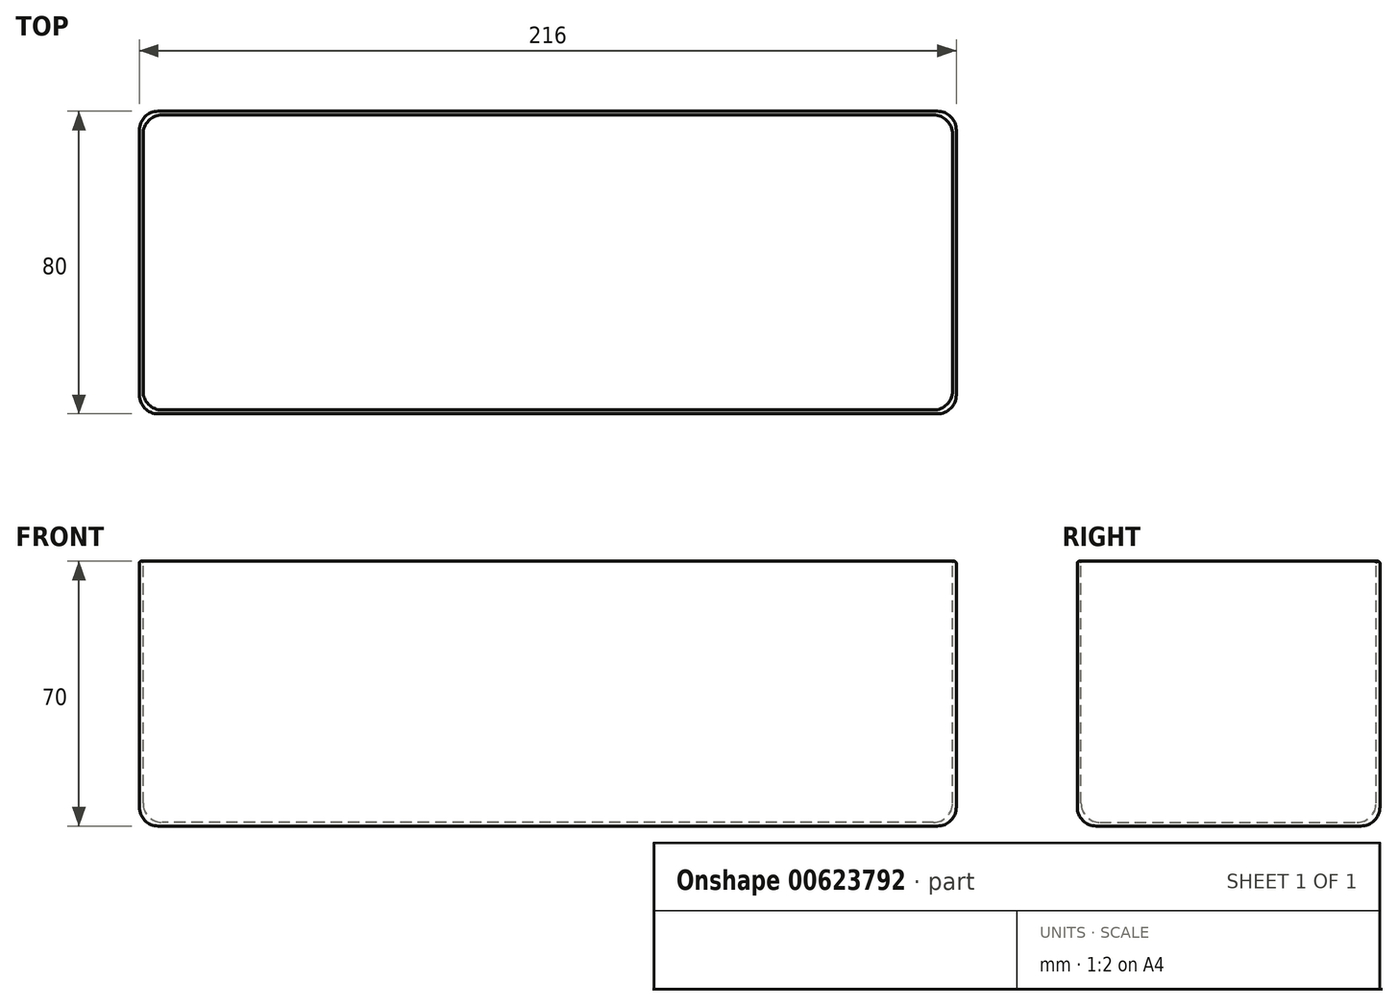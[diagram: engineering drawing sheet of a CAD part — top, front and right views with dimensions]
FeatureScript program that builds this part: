
annotation { "Feature Type Name" : "Feature", "Feature Type Description" : "" }
export const myFeature = defineFeature(function(context is Context, id is Id, definition is map)
    precondition{}
    {
        {
            var Q0;
            Q0=qCreatedBy(makeId("Top.planeOp"),FACE);
            var sketch = newSketch(context, id + "F0", { "sketchPlane" : qUnion([Q0])});
            skLineSegment(sketch, "E0.bottom", {"start": v(108, -40) * mm, "end": v(-108, -40) * mm});
            skLineSegment(sketch, "E0.top", {"start": v(108, 40) * mm, "end": v(-108, 40) * mm});
            skLineSegment(sketch, "E0.left", {"start": v(108, -40) * mm, "end": v(108, 40) * mm});
            skLineSegment(sketch, "E0.right", {"start": v(-108, -40) * mm, "end": v(-108, 40) * mm});
            skPoint(sketch, "E0.middle", {"position": v(0, 0) * mm});
            skSolve(sketch);
        }
        {
            var Q0;
            Q0=makeQuery(id+"F0.imprint","IMPRINT",FACE,{"disambiguationData":[TD([[makeQuery(id+"F0.imprint","IMPRINT",EDGE,{"derivedFrom":sQuery(id+"F0.wireOp",EDGE,"E0.bottom")}),-1.0]])]});
            extrude(context, id + "F1", {"entities" : qUnion([Q0]), "depth" : 70 * mm, "offsetDistance" : 25 * mm});
        }
        {
            var Q0;
            Q0=makeQuery(id+"F1.opExtrude","CAP_FACE",FACE,{"disambiguationData":[OSD([sQuery(id+"F0.wireOp",EDGE,"E0.bottom"),sQuery(id+"F0.wireOp",EDGE,"E0.top"),sQuery(id+"F0.wireOp",EDGE,"E0.left"),sQuery(id+"F0.wireOp",EDGE,"E0.right")])],"isStart":false});
            var sketch = newSketch(context, id + "F2", { "sketchPlane" : qUnion([Q0])});
            skLineSegment(sketch, "E1.bottom", {"start": v(107, -39) * mm, "end": v(-107, -39) * mm});
            skLineSegment(sketch, "E1.top", {"start": v(107, 39) * mm, "end": v(-107, 39) * mm});
            skLineSegment(sketch, "E1.left", {"start": v(107, -39) * mm, "end": v(107, 39) * mm});
            skLineSegment(sketch, "E1.right", {"start": v(-107, -39) * mm, "end": v(-107, 39) * mm});
            skPoint(sketch, "E1.middle", {"position": v(0, 0) * mm});
            skSolve(sketch);
        }
        {
            var Q0;
            Q0=makeQuery(id+"F2.imprint","IMPRINT",FACE,{"disambiguationData":[TD([[makeQuery(id+"F2.imprint","IMPRINT",EDGE,{"derivedFrom":sQuery(id+"F2.wireOp",EDGE,"E1.bottom")}),-1.0]])]});
            extrude(context, id + "F3", {"entities" : qUnion([Q0]), "operationType" : NewBodyOperationType.REMOVE, "oppositeDirection" : true, "depth" : 69 * mm, "offsetDistance" : 25 * mm});
        }
        {
            var Q0;
            Q0=makeQuery(id+"F3.boolean.opBoolean","COPY",EDGE,{"derivedFrom":makeQuery(id+"F3.opExtrude","SWEPT_EDGE",EDGE,{"disambiguationData":[OSD([sQuery(id+"F2.wireOp",EDGE,"E1.top"),sQuery(id+"F2.wireOp",EDGE,"E1.right")])]})});
            var Q1;
            Q1=makeQuery(id+"F3.boolean.opBoolean","COPY",EDGE,{"derivedFrom":makeQuery(id+"F3.opExtrude","SWEPT_EDGE",EDGE,{"disambiguationData":[OSD([sQuery(id+"F2.wireOp",EDGE,"E1.bottom"),sQuery(id+"F2.wireOp",EDGE,"E1.right")])]})});
            var Q2;
            Q2=makeQuery(id+"F3.boolean.opBoolean","COPY",EDGE,{"derivedFrom":makeQuery(id+"F3.opExtrude","SWEPT_EDGE",EDGE,{"disambiguationData":[OSD([sQuery(id+"F2.wireOp",EDGE,"E1.bottom"),sQuery(id+"F2.wireOp",EDGE,"E1.left")])]})});
            var Q3;
            Q3=makeQuery(id+"F3.boolean.opBoolean","COPY",EDGE,{"derivedFrom":makeQuery(id+"F3.opExtrude","SWEPT_EDGE",EDGE,{"disambiguationData":[OSD([sQuery(id+"F2.wireOp",EDGE,"E1.top"),sQuery(id+"F2.wireOp",EDGE,"E1.left")])]})});
            var Q4;
            Q4=makeQuery(id+"F3.boolean.opBoolean","COPY",FACE,{"derivedFrom":makeQuery(id+"F3.opExtrude","CAP_FACE",FACE,{"disambiguationData":[OSD([sQuery(id+"F2.wireOp",EDGE,"E1.bottom"),sQuery(id+"F2.wireOp",EDGE,"E1.top"),sQuery(id+"F2.wireOp",EDGE,"E1.left"),sQuery(id+"F2.wireOp",EDGE,"E1.right")])],"isStart":false})});
            var Q5;
            Q5=makeQuery(id+"F1.opExtrude","CAP_EDGE",EDGE,{"disambiguationData":[OSD([sQuery(id+"F0.wireOp",EDGE,"E0.bottom")])],"isStart":true});
            fillet(context, id + "F4", {"entities" : qUnion([Q0, Q1, Q2, Q3, Q4, Q5]), "radius" : 5 * mm, "tangentPropagation" : true, "allowEdgeOverflow" : false});
        }
        {
            var Q0;
            {var subQ0=sQuery(id+"F0.wireOp",EDGE,"E0.bottom");Q0=makeQuery(id+"F4.opFillet","BLEND_EDGE",EDGE,{"blendedFrom":[makeQuery(id+"F1.opExtrude","CAP_EDGE",EDGE,{"disambiguationData":[OSD([subQ0])],"isStart":true}),makeQuery(id+"F1.opExtrude","SWEPT_FACE",FACE,{"disambiguationData":[OSD([subQ0])]})],"blendedInto":[makeQuery(id+"F1.opExtrude","SWEPT_FACE",FACE,{"disambiguationData":[OSD([subQ0])]})]});}
            var Q1;
            Q1=makeQuery(id+"F1.opExtrude","SWEPT_EDGE",EDGE,{"disambiguationData":[OSD([sQuery(id+"F0.wireOp",EDGE,"E0.bottom"),sQuery(id+"F0.wireOp",EDGE,"E0.right")])]});
            var Q2;
            Q2=makeQuery(id+"F1.opExtrude","SWEPT_EDGE",EDGE,{"disambiguationData":[OSD([sQuery(id+"F0.wireOp",EDGE,"E0.top"),sQuery(id+"F0.wireOp",EDGE,"E0.right")])]});
            var Q3;
            Q3=makeQuery(id+"F1.opExtrude","CAP_EDGE",EDGE,{"disambiguationData":[OSD([sQuery(id+"F0.wireOp",EDGE,"E0.left")])],"isStart":true});
            var Q4;
            Q4=makeQuery(id+"F1.opExtrude","SWEPT_EDGE",EDGE,{"disambiguationData":[OSD([sQuery(id+"F0.wireOp",EDGE,"E0.top"),sQuery(id+"F0.wireOp",EDGE,"E0.left")])]});
            var Q5;
            Q5=makeQuery(id+"F1.opExtrude","CAP_EDGE",EDGE,{"disambiguationData":[OSD([sQuery(id+"F0.wireOp",EDGE,"E0.top")])],"isStart":true});
            fillet(context, id + "F5", {"entities" : qUnion([Q0, Q1, Q2, Q3, Q4, Q5]), "radius" : 5 * mm, "tangentPropagation" : true, "allowEdgeOverflow" : false});
        }
        {
            var Q0;
            Q0=makeQuery(id+"F1.opExtrude","CAP_EDGE",EDGE,{"disambiguationData":[OSD([sQuery(id+"F0.wireOp",EDGE,"E0.top")])],"isStart":false});
            var Q1;
            Q1=makeQuery(id+"F3.boolean.opBoolean","COPY",EDGE,{"derivedFrom":makeQuery(id+"F3.opExtrude","CAP_EDGE",EDGE,{"disambiguationData":[OSD([sQuery(id+"F2.wireOp",EDGE,"E1.bottom")])],"isStart":true})});
            var Q2;
            Q2=makeQuery(id+"F3.boolean.opBoolean","COPY",EDGE,{"derivedFrom":makeQuery(id+"F3.opExtrude","CAP_EDGE",EDGE,{"disambiguationData":[OSD([sQuery(id+"F2.wireOp",EDGE,"E1.top")])],"isStart":true})});
            var Q3;
            Q3=makeQuery(id+"F3.boolean.opBoolean","COPY",EDGE,{"derivedFrom":makeQuery(id+"F3.opExtrude","CAP_EDGE",EDGE,{"disambiguationData":[OSD([sQuery(id+"F2.wireOp",EDGE,"E1.left")])],"isStart":true})});
            var Q4;
            Q4=makeQuery(id+"F4.opFillet","BLEND_EDGE",EDGE,{"blendedFrom":[makeQuery(id+"F3.boolean.opBoolean","COPY",EDGE,{"derivedFrom":makeQuery(id+"F3.opExtrude","SWEPT_EDGE",EDGE,{"disambiguationData":[OSD([sQuery(id+"F2.wireOp",EDGE,"E1.bottom"),sQuery(id+"F2.wireOp",EDGE,"E1.right")])]})}),makeQuery(id+"F1.opExtrude","CAP_FACE",FACE,{"disambiguationData":[OSD([sQuery(id+"F0.wireOp",EDGE,"E0.bottom"),sQuery(id+"F0.wireOp",EDGE,"E0.top"),sQuery(id+"F0.wireOp",EDGE,"E0.left"),sQuery(id+"F0.wireOp",EDGE,"E0.right")])],"isStart":false})],"blendedInto":[makeQuery(id+"F1.opExtrude","CAP_FACE",FACE,{"disambiguationData":[OSD([sQuery(id+"F0.wireOp",EDGE,"E0.bottom"),sQuery(id+"F0.wireOp",EDGE,"E0.top"),sQuery(id+"F0.wireOp",EDGE,"E0.left"),sQuery(id+"F0.wireOp",EDGE,"E0.right")])],"isStart":false})]});
            var Q5;
            Q5=makeQuery(id+"F3.boolean.opBoolean","COPY",EDGE,{"derivedFrom":makeQuery(id+"F3.opExtrude","CAP_EDGE",EDGE,{"disambiguationData":[OSD([sQuery(id+"F2.wireOp",EDGE,"E1.right")])],"isStart":true})});
            var Q6;
            Q6=makeQuery(id+"F4.opFillet","BLEND_EDGE",EDGE,{"blendedFrom":[makeQuery(id+"F3.boolean.opBoolean","COPY",EDGE,{"derivedFrom":makeQuery(id+"F3.opExtrude","SWEPT_EDGE",EDGE,{"disambiguationData":[OSD([sQuery(id+"F2.wireOp",EDGE,"E1.top"),sQuery(id+"F2.wireOp",EDGE,"E1.left")])]})}),makeQuery(id+"F1.opExtrude","CAP_FACE",FACE,{"disambiguationData":[OSD([sQuery(id+"F0.wireOp",EDGE,"E0.bottom"),sQuery(id+"F0.wireOp",EDGE,"E0.top"),sQuery(id+"F0.wireOp",EDGE,"E0.left"),sQuery(id+"F0.wireOp",EDGE,"E0.right")])],"isStart":false})],"blendedInto":[makeQuery(id+"F1.opExtrude","CAP_FACE",FACE,{"disambiguationData":[OSD([sQuery(id+"F0.wireOp",EDGE,"E0.bottom"),sQuery(id+"F0.wireOp",EDGE,"E0.top"),sQuery(id+"F0.wireOp",EDGE,"E0.left"),sQuery(id+"F0.wireOp",EDGE,"E0.right")])],"isStart":false})]});
            var Q7;
            Q7=makeQuery(id+"F1.opExtrude","CAP_EDGE",EDGE,{"disambiguationData":[OSD([sQuery(id+"F0.wireOp",EDGE,"E0.bottom")])],"isStart":false});
            var Q8;
            Q8=makeQuery(id+"F1.opExtrude","CAP_EDGE",EDGE,{"disambiguationData":[OSD([sQuery(id+"F0.wireOp",EDGE,"E0.left")])],"isStart":false});
            var Q9;
            {var subQ0=sQuery(id+"F0.wireOp",EDGE,"E0.left");var subQ1=sQuery(id+"F0.wireOp",EDGE,"E0.bottom");Q9=makeQuery(id+"F5.opFillet","BLEND_EDGE",EDGE,{"blendedFrom":[makeQuery(id+"F1.opExtrude","SWEPT_EDGE",EDGE,{"disambiguationData":[OSD([subQ1,subQ0])]}),makeQuery(id+"F1.opExtrude","CAP_FACE",FACE,{"disambiguationData":[OSD([subQ1,sQuery(id+"F0.wireOp",EDGE,"E0.top"),subQ0,sQuery(id+"F0.wireOp",EDGE,"E0.right")])],"isStart":false})],"blendedInto":[makeQuery(id+"F1.opExtrude","CAP_FACE",FACE,{"disambiguationData":[OSD([subQ1,sQuery(id+"F0.wireOp",EDGE,"E0.top"),subQ0,sQuery(id+"F0.wireOp",EDGE,"E0.right")])],"isStart":false})]});}
            var Q10;
            Q10=makeQuery(id+"F1.opExtrude","CAP_EDGE",EDGE,{"disambiguationData":[OSD([sQuery(id+"F0.wireOp",EDGE,"E0.right")])],"isStart":false});
            var Q11;
            Q11=makeQuery(id+"F1.opExtrude","CAP_FACE",FACE,{"disambiguationData":[OSD([sQuery(id+"F0.wireOp",EDGE,"E0.bottom"),sQuery(id+"F0.wireOp",EDGE,"E0.top"),sQuery(id+"F0.wireOp",EDGE,"E0.left"),sQuery(id+"F0.wireOp",EDGE,"E0.right")])],"isStart":false});
            var Q12;
            {var subQ0=sQuery(id+"F0.wireOp",EDGE,"E0.right");var subQ1=sQuery(id+"F0.wireOp",EDGE,"E0.bottom");Q12=makeQuery(id+"F5.opFillet","BLEND_EDGE",EDGE,{"blendedFrom":[makeQuery(id+"F1.opExtrude","SWEPT_EDGE",EDGE,{"disambiguationData":[OSD([subQ1,subQ0])]}),makeQuery(id+"F1.opExtrude","CAP_FACE",FACE,{"disambiguationData":[OSD([subQ1,sQuery(id+"F0.wireOp",EDGE,"E0.top"),sQuery(id+"F0.wireOp",EDGE,"E0.left"),subQ0])],"isStart":false})],"blendedInto":[makeQuery(id+"F1.opExtrude","CAP_FACE",FACE,{"disambiguationData":[OSD([subQ1,sQuery(id+"F0.wireOp",EDGE,"E0.top"),sQuery(id+"F0.wireOp",EDGE,"E0.left"),subQ0])],"isStart":false})]});}
            var Q13;
            Q13=makeQuery(id+"F4.opFillet","BLEND_EDGE",EDGE,{"blendedFrom":[makeQuery(id+"F3.boolean.opBoolean","COPY",EDGE,{"derivedFrom":makeQuery(id+"F3.opExtrude","SWEPT_EDGE",EDGE,{"disambiguationData":[OSD([sQuery(id+"F2.wireOp",EDGE,"E1.top"),sQuery(id+"F2.wireOp",EDGE,"E1.right")])]})}),makeQuery(id+"F1.opExtrude","CAP_FACE",FACE,{"disambiguationData":[OSD([sQuery(id+"F0.wireOp",EDGE,"E0.bottom"),sQuery(id+"F0.wireOp",EDGE,"E0.top"),sQuery(id+"F0.wireOp",EDGE,"E0.left"),sQuery(id+"F0.wireOp",EDGE,"E0.right")])],"isStart":false})],"blendedInto":[makeQuery(id+"F1.opExtrude","CAP_FACE",FACE,{"disambiguationData":[OSD([sQuery(id+"F0.wireOp",EDGE,"E0.bottom"),sQuery(id+"F0.wireOp",EDGE,"E0.top"),sQuery(id+"F0.wireOp",EDGE,"E0.left"),sQuery(id+"F0.wireOp",EDGE,"E0.right")])],"isStart":false})]});
            var Q14;
            Q14=makeQuery(id+"F4.opFillet","BLEND_EDGE",EDGE,{"blendedFrom":[makeQuery(id+"F3.boolean.opBoolean","COPY",EDGE,{"derivedFrom":makeQuery(id+"F3.opExtrude","SWEPT_EDGE",EDGE,{"disambiguationData":[OSD([sQuery(id+"F2.wireOp",EDGE,"E1.bottom"),sQuery(id+"F2.wireOp",EDGE,"E1.left")])]})}),makeQuery(id+"F1.opExtrude","CAP_FACE",FACE,{"disambiguationData":[OSD([sQuery(id+"F0.wireOp",EDGE,"E0.bottom"),sQuery(id+"F0.wireOp",EDGE,"E0.top"),sQuery(id+"F0.wireOp",EDGE,"E0.left"),sQuery(id+"F0.wireOp",EDGE,"E0.right")])],"isStart":false})],"blendedInto":[makeQuery(id+"F1.opExtrude","CAP_FACE",FACE,{"disambiguationData":[OSD([sQuery(id+"F0.wireOp",EDGE,"E0.bottom"),sQuery(id+"F0.wireOp",EDGE,"E0.top"),sQuery(id+"F0.wireOp",EDGE,"E0.left"),sQuery(id+"F0.wireOp",EDGE,"E0.right")])],"isStart":false})]});
            var Q15;
            {var subQ0=sQuery(id+"F0.wireOp",EDGE,"E0.left");var subQ1=sQuery(id+"F0.wireOp",EDGE,"E0.top");Q15=makeQuery(id+"F5.opFillet","BLEND_EDGE",EDGE,{"blendedFrom":[makeQuery(id+"F1.opExtrude","SWEPT_EDGE",EDGE,{"disambiguationData":[OSD([subQ1,subQ0])]}),makeQuery(id+"F1.opExtrude","CAP_FACE",FACE,{"disambiguationData":[OSD([sQuery(id+"F0.wireOp",EDGE,"E0.bottom"),subQ1,subQ0,sQuery(id+"F0.wireOp",EDGE,"E0.right")])],"isStart":false})],"blendedInto":[makeQuery(id+"F1.opExtrude","CAP_FACE",FACE,{"disambiguationData":[OSD([sQuery(id+"F0.wireOp",EDGE,"E0.bottom"),subQ1,subQ0,sQuery(id+"F0.wireOp",EDGE,"E0.right")])],"isStart":false})]});}
            var Q16;
            {var subQ0=sQuery(id+"F0.wireOp",EDGE,"E0.right");var subQ1=sQuery(id+"F0.wireOp",EDGE,"E0.top");Q16=makeQuery(id+"F5.opFillet","BLEND_EDGE",EDGE,{"blendedFrom":[makeQuery(id+"F1.opExtrude","SWEPT_EDGE",EDGE,{"disambiguationData":[OSD([subQ1,subQ0])]}),makeQuery(id+"F1.opExtrude","CAP_FACE",FACE,{"disambiguationData":[OSD([sQuery(id+"F0.wireOp",EDGE,"E0.bottom"),subQ1,sQuery(id+"F0.wireOp",EDGE,"E0.left"),subQ0])],"isStart":false})],"blendedInto":[makeQuery(id+"F1.opExtrude","CAP_FACE",FACE,{"disambiguationData":[OSD([sQuery(id+"F0.wireOp",EDGE,"E0.bottom"),subQ1,sQuery(id+"F0.wireOp",EDGE,"E0.left"),subQ0])],"isStart":false})]});}
            fillet(context, id + "F6", {"entities" : qUnion([Q0, Q1, Q2, Q3, Q4, Q5, Q6, Q7, Q8, Q9, Q10, Q11, Q12, Q13, Q14, Q15, Q16]), "radius" : .5 * mm, "tangentPropagation" : true, "allowEdgeOverflow" : false});
        }
    });
